# Revit family: WIR-GATEWAY3
name_source: partatom
category: Communication Devices
units: mm (PartAtom-declared; Revit-internal decimal feet)

## family parameters
Cut with Voids When Loaded = No
Host = Face
Maintain Annotation Orientation = No
OmniClass Number = 23.85.80.11.27
OmniClass Title = Lighting Controls
Part Type = Normal
Room Calculation Point = No
Round Connector Dimension = Use Diameter
Shared = Yes

## types (1)
- WIR-GATEWAY3
    Assembly Code = D5090
    Default Elevation = 48 "
    Description = Control Solutions' wiSCAPE® Gateway G3 (GW3) is a completely autonomous controller used to combine wiSCAPE Fixture Modules into a single wireless network. The GW3 enables communications between wiSCAPE fixture modules and the wiSCAPE Enterprise Central Management Server or the wiSCAPE Expresssoftware application. Although each fixture module is functionally autonomous, the GW3 acts as an access point through which the modules can be managed, monitored and metered. The GW3 then sends the data obtained from the fixture modules to the wiSCAPE Enterprise Central Management Server which collects the data from multiple gateways.
    Features = Autonomously manages up to 1000 fixture modules (500 recommended)
• Astronomical and fixed time scheduling
• Uses Flash memory storage in order to withstand temperature, shock
and vibrations
• Supports network connectivity via Ethernet connection (Standard)
or optional cellular modem
• Surge protected
• NEMA 4X (IP66) cabinet
• Secure communication using AES-128 encryption
• Optional cabinet heater for extreme cold environments
    Housing Material = Paint - Machined Aluminum
    Manufacturer = NX Lighting Controls
    Model = WIR-GATEWAY3
    Type Comments = Bluetooth® Radio Controller
    URL = https://www.currentlighting.com
    Warranty = 5-Years Warranty

## geometry (parser evidence)
native form markers: Sweep x3
no freeform markers — native parametric forms only
